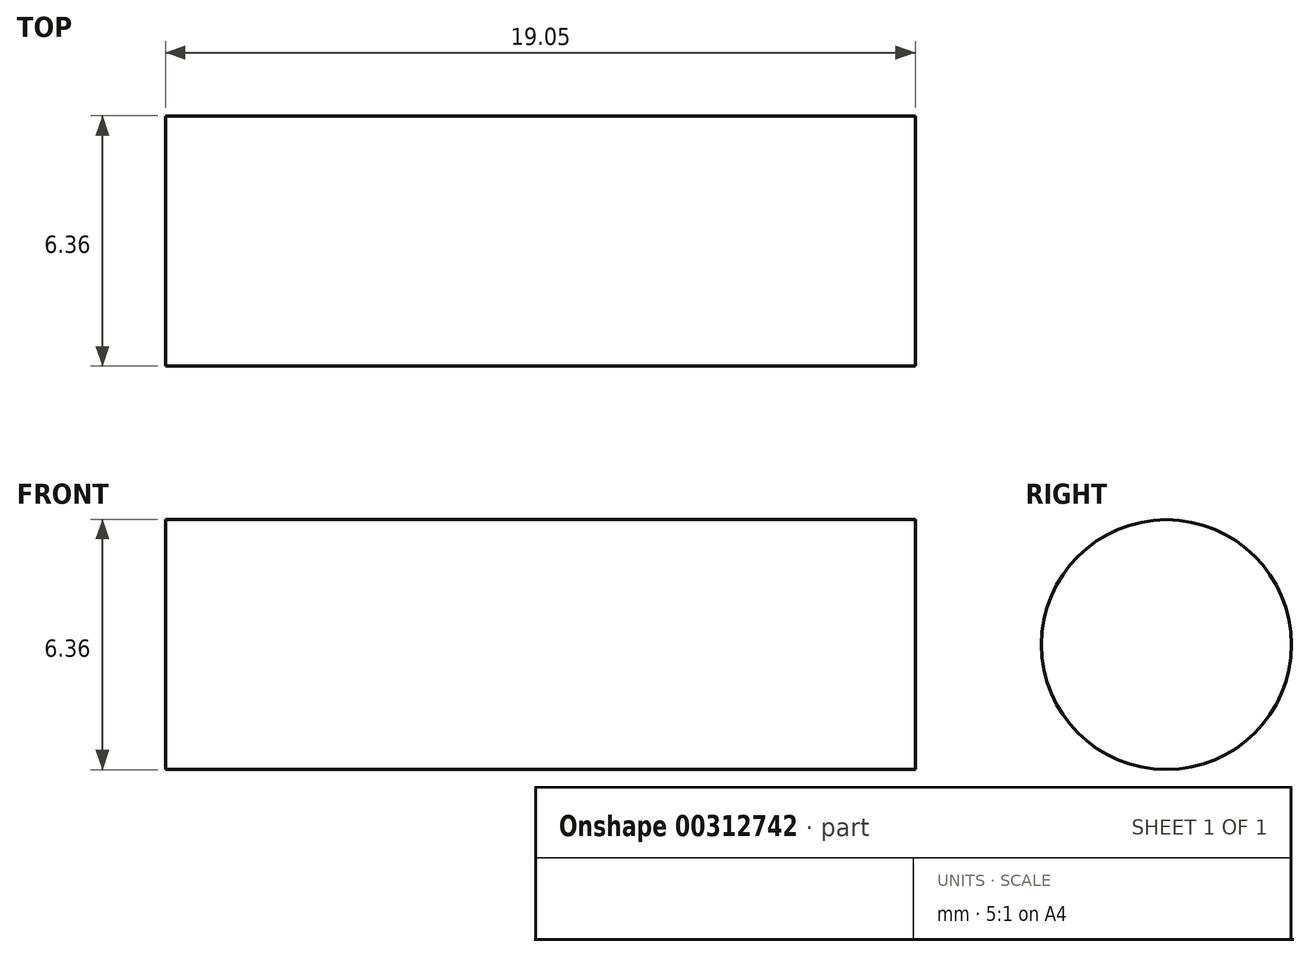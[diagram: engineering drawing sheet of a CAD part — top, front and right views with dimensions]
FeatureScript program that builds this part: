
annotation { "Feature Type Name" : "Feature", "Feature Type Description" : "" }
export const myFeature = defineFeature(function(context is Context, id is Id, definition is map)
    precondition{}
    {
        {
            var Q0;
            Q0=qCreatedBy(makeId("Right.planeOp"),FACE);
            var sketch = newSketch(context, id + "F0", { "sketchPlane" : qUnion([Q0])});
            skCircle(sketch, "E0", {"center": v(0, 0) * mm, "radius": 3.17 * mm});
            skSolve(sketch);
        }
        {
            var Q0;
            Q0=makeQuery(id+"F0.imprint","IMPRINT",FACE,{"disambiguationData":[TD([[makeQuery(id+"F0.imprint","IMPRINT",EDGE,{"derivedFrom":sQuery(id+"F0.wireOp",EDGE,"E0")}),1.0]])]});
            extrude(context, id + "F1", {"entities" : qUnion([Q0]), "depth" : 19.05 * mm});
        }
    });
